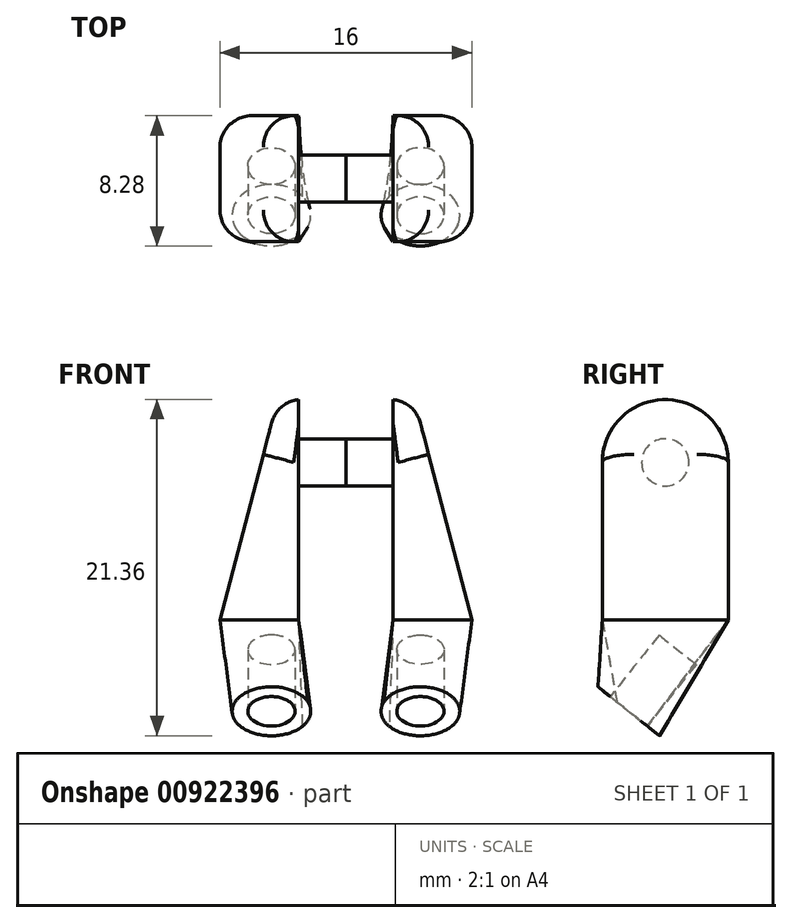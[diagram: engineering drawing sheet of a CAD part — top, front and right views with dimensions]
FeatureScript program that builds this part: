
annotation { "Feature Type Name" : "Feature", "Feature Type Description" : "" }
export const myFeature = defineFeature(function(context is Context, id is Id, definition is map)
    precondition{}
    {
        {
            var Q0;
            Q0=qCreatedBy(makeId("Right.planeOp"),FACE);
            var sketch = newSketch(context, id + "F0", { "sketchPlane" : qUnion([Q0])});
            skCircle(sketch, "E0", {"center": v(0, 0) * mm, "radius": 1.5 * mm});
            skSolve(sketch);
        }
        {
            var Q0;
            Q0=qSketchRegion(id+"F0",true);
            extrude(context, id + "F1", {"entities" : qUnion([Q0]), "depth" : 3 * mm});
        }
        {
            var Q0;
            Q0=makeQuery(id+"F1.opExtrude","CAP_FACE",FACE,{"disambiguationData":[OSD([sQuery(id+"F0.wireOp",EDGE,"E0")])],"isStart":false});
            var sketch = newSketch(context, id + "F2", { "sketchPlane" : qUnion([Q0])});
            skArc(sketch, "E1", {"start": v(4, 0) * mm, "mid": v(0, 4) * mm, "end": v(-4, 0) * mm});
            skLineSegment(sketch, "E2.top", {"start": v(4, -10) * mm, "end": v(-4, -10) * mm});
            skLineSegment(sketch, "E2.left", {"start": v(4, 0) * mm, "end": v(4, -10) * mm});
            skLineSegment(sketch, "E2.right", {"start": v(-4, 0) * mm, "end": v(-4, -10) * mm});
            skPoint(sketch, "E2.middle", {"position": v(0, -5) * mm});
            skLineSegment(sketch, "E3", {"start": v(4, -10) * mm, "end": v(-1.29, -16.64) * mm, "construction": true});
            skLineSegment(sketch, "E4", {"start": v(-1.29, -16.64) * mm, "end": v(-6.18, -12.74) * mm, "construction": true});
            skLineSegment(sketch, "E5", {"start": v(-6.18, -12.74) * mm, "end": v(-4, -10) * mm, "construction": true});
            skLineSegment(sketch, "E6", {"start": v(-3.73, -14.69) * mm, "end": v(-1.56, -11.96) * mm, "construction": true});
            skSolve(sketch);
        }
        {
            var Q0;
            Q0=qSketchRegion(id+"F2",true);
            extrude(context, id + "F3", {"entities" : qUnion([Q0]), "operationType" : NewBodyOperationType.ADD, "depth" : 5 * mm});
        }
        {
            var Q0;
            Q0=makeQuery(id+"F3.opExtrude","SWEPT_FACE",FACE,{"disambiguationData":[OSD([sQuery(id+"F2.wireOp",EDGE,"E2.right")])]});
            var sketch = newSketch(context, id + "F4", { "sketchPlane" : qUnion([Q0])});
            skLineSegment(sketch, "E7", {"start": v(8, -10) * mm, "end": v(4.2, 4.5) * mm});
            skLineSegment(sketch, "E8", {"start": v(4.2, 4.5) * mm, "end": v(11.03, 4.5) * mm});
            skLineSegment(sketch, "E9", {"start": v(11.03, 4.5) * mm, "end": v(8, -10) * mm});
            skSolve(sketch);
        }
        {
            var Q0;
            Q0=qSketchRegion(id+"F4",true);
            extrude(context, id + "F5", {"entities" : qUnion([Q0]), "operationType" : NewBodyOperationType.REMOVE, "oppositeDirection" : true, "depth" : 25 * mm});
        }
        {
            var Q0;
            Q0=makeQuery(id+"F5.boolean.opBoolean","INTERSECT",EDGE,{"derivedFrom":[makeQuery(id+"F3.opExtrude","SWEPT_FACE",FACE,{"disambiguationData":[OSD([sQuery(id+"F2.wireOp",EDGE,"E1")])]}),makeQuery(id+"F5.opExtrude","SWEPT_FACE",FACE,{"disambiguationData":[OSD([sQuery(id+"F4.wireOp",EDGE,"E7")])]})]});
            var Q1;
            Q1=makeQuery(id+"F5.boolean.opBoolean","INTERSECT",EDGE,{"derivedFrom":[makeQuery(id+"F3.opExtrude","SWEPT_FACE",FACE,{"disambiguationData":[OSD([sQuery(id+"F2.wireOp",EDGE,"E2.left")])]}),makeQuery(id+"F5.opExtrude","SWEPT_FACE",FACE,{"disambiguationData":[OSD([sQuery(id+"F4.wireOp",EDGE,"E7")])]})]});
            fillet(context, id + "F6", {"entities" : qUnion([Q0, Q1]), "radius" : 2 * mm, "tangentPropagation" : true, "allowEdgeOverflow" : false});
        }
        {
            var Q0;
            Q0=sQuery(id+"F2.wireOp",VERTEX,"E5.start");
            var Q1;
            Q1=sQuery(id+"F2.wireOp",EDGE,"E5");
            cPlane(context, id + "F7", {"entities" : qUnion([Q0, Q1]), "cplaneType" : CPlaneType.LINE_POINT, "offset" : 150 * mm, "width" : 150 * mm, "height" : 150 * mm});
        }
        {
            var Q0;
            Q0=qCreatedBy(id+"F7.planeOp",FACE);
            var sketch = newSketch(context, id + "F8", { "sketchPlane" : qUnion([Q0])});
            skLineSegment(sketch, "E10", {"start": v(3, 6.23) * mm, "end": v(8.1, 11.55) * mm, "construction": true});
            skCircle(sketch, "E11", {"center": v(4.73, 8.04) * mm, "radius": 2.5 * mm});
            skSolve(sketch);
        }
        {
            var Q1;
            Q1=makeQuery(id+"F3.opExtrude","SWEPT_FACE",FACE,{"disambiguationData":[OSD([sQuery(id+"F2.wireOp",EDGE,"E2.top")])]});
            var Q2;
            Q2=makeQuery(id+"F8.imprint","IMPRINT",FACE,{"disambiguationData":[TD([[makeQuery(id+"F8.imprint","IMPRINT",EDGE,{"derivedFrom":sQuery(id+"F8.wireOp",EDGE,"E11")}),1.0]])]});
            loft(context, id + "F9", {"operationType" : NewBodyOperationType.ADD, "sheetProfilesArray" : [{ "sheetProfileEntities" : qUnion([Q1]) }, { "sheetProfileEntities" : qUnion([Q2]) }]});
        }
        {
            var Q0;
            Q0=makeQuery(id+"F8.imprint","IMPRINT",FACE,{"disambiguationData":[TD([[makeQuery(id+"F8.imprint","IMPRINT",EDGE,{"derivedFrom":sQuery(id+"F8.wireOp",EDGE,"E11")}),1.0]])]});
            var sketch = newSketch(context, id + "F10", { "sketchPlane" : qUnion([Q0])});
            skCircle(sketch, "E12", {"center": v(4.73, 8.04) * mm, "radius": 1.5 * mm});
            skSolve(sketch);
        }
        {
            var Q0;
            Q0=qSketchRegion(id+"F10",true);
            extrude(context, id + "F11", {"entities" : qUnion([Q0]), "operationType" : NewBodyOperationType.REMOVE, "depth" : 5 * mm});
        }
        {
            var Q0;
            Q0=makeQuery(id+"F1.opExtrude","SWEPT_BODY",BODY,{"disambiguationData":[OSD([sQuery(id+"F0.wireOp",EDGE,"E0")])]});
            var Q1;
            Q1=makeQuery(id+"F1.opExtrude","CAP_FACE",FACE,{"disambiguationData":[OSD([sQuery(id+"F0.wireOp",EDGE,"E0")])],"isStart":true});
            mirror(context, id + "F12", {"entities" : qUnion([Q0]), "mirrorPlane" : qUnion([Q1])});
        }
        {
            var Q0;
            Q0=makeQuery(id+"F1.opExtrude","SWEPT_BODY",BODY,{"disambiguationData":[OSD([sQuery(id+"F0.wireOp",EDGE,"E0")])]});
            transform(context, id + "F13", {"entities" : qUnion([Q0]), "transformType" : TransformType.TRANSLATION_3D, "dx" : 0 * mm, "dy" : 0 * mm, "dz" : 0 * mm, "makeCopy" : true});
        }
    });
